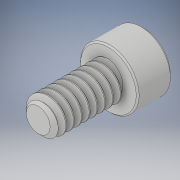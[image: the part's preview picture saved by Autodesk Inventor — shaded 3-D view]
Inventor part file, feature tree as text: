
AUTODESK INVENTOR PART (.ipt)
format: ipt  version: 2018 (Build 220112000, 112)  size: 645,632 bytes
history: native  units: in
note: dims shown in document units (in); Inventor stores cm internally (conversion verified against a paired STEP export)
features: chamfer x1
ambient origin geometry x8: Origin, YZ Plane, XZ Plane, XY Plane, X Axis, Y Axis, Z Axis, Center Point
bodies: Solid1 (feature_tree)
feature tree (1):
  chamfer  "Chamfer2"  [1 undecoded]
note: 1 required parameter value undecoded (feature->parameter linkage not recoverable at this tier; creation-order binding heuristic only, values carry confidence <= 0.55)
